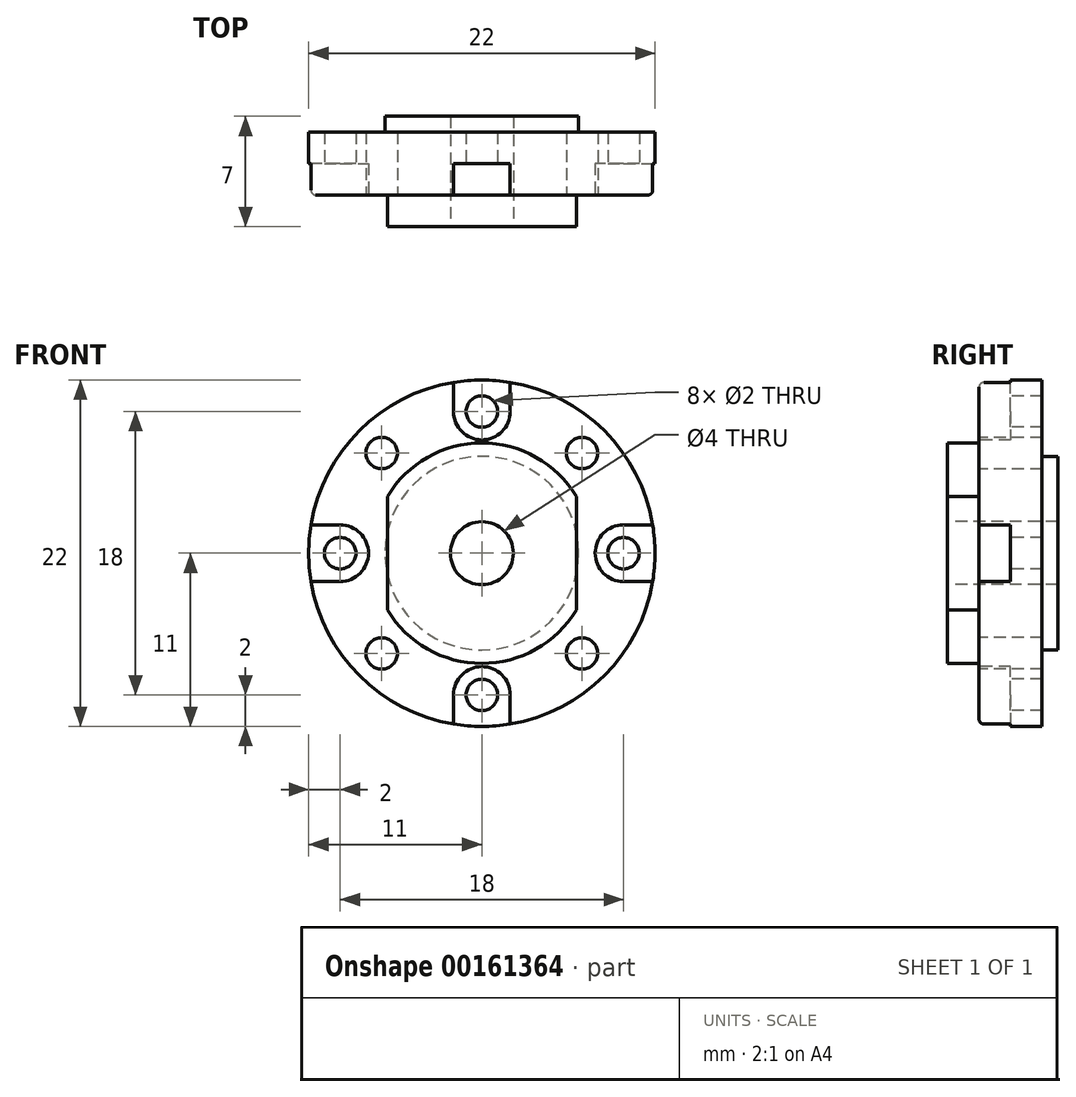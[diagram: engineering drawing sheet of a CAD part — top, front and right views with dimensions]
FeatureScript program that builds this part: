
annotation { "Feature Type Name" : "Feature", "Feature Type Description" : "" }
export const myFeature = defineFeature(function(context is Context, id is Id, definition is map)
    precondition{}
    {
        {
            var Q0;
            Q0=qCreatedBy(makeId("Front.planeOp"),FACE);
            var sketch = newSketch(context, id + "F0", { "sketchPlane" : qUnion([Q0])});
            skCircle(sketch, "E0", {"center": v(0, 0) * mm, "radius": 11 * mm});
            skSolve(sketch);
        }
        {
            var Q0;
            Q0=qSketchRegion(id+"F0",true);
            extrude(context, id + "F1", {"entities" : qUnion([Q0]), "depth" : 6 * mm});
        }
        {
            var Q0;
            Q0=makeQuery(id+"F1.opExtrude","CAP_FACE",FACE,{"disambiguationData":[OSD([sQuery(id+"F0.wireOp",EDGE,"E0")])],"isStart":false});
            var sketch = newSketch(context, id + "F2", { "sketchPlane" : qUnion([Q0])});
            skArc(sketch, "E1", {"start": v(-6, -3.6) * mm, "mid": v(0, -7) * mm, "end": v(6, -3.6) * mm});
            skCircle(sketch, "E2", {"center": v(0, 0) * mm, "radius": 16 * mm});
            skLineSegment(sketch, "E3", {"start": v(-6, 3.6) * mm, "end": v(-6, -3.6) * mm});
            skLineSegment(sketch, "E4", {"start": v(6, 3.6) * mm, "end": v(6, -3.6) * mm});
            skArc(sketch, "E5.trimOffspring", {"start": v(6, 3.6) * mm, "mid": v(0, 7) * mm, "end": v(-6, 3.6) * mm});
            skSolve(sketch);
        }
        {
            var Q0;
            Q0=qSketchRegion(id+"F2",true);
            extrude(context, id + "F3", {"entities" : qUnion([Q0]), "operationType" : NewBodyOperationType.REMOVE, "oppositeDirection" : true, "depth" : 2 * mm});
        }
        {
            var Q0;
            Q0=makeQuery(id+"F1.opExtrude","CAP_FACE",FACE,{"disambiguationData":[OSD([sQuery(id+"F0.wireOp",EDGE,"E0")])],"isStart":false});
            var sketch = newSketch(context, id + "F4", { "sketchPlane" : qUnion([Q0])});
            skCircle(sketch, "E6", {"center": v(0, 0) * mm, "radius": 2 * mm});
            skSolve(sketch);
        }
        {
            var Q0;
            Q0=makeQuery(id+"F3.boolean.opBoolean","COPY",FACE,{"derivedFrom":makeQuery(id+"F3.opExtrude","CAP_FACE",FACE,{"disambiguationData":[OSD([sQuery(id+"F2.wireOp",EDGE,"E1"),sQuery(id+"F2.wireOp",EDGE,"E2"),sQuery(id+"F2.wireOp",EDGE,"E3"),sQuery(id+"F2.wireOp",EDGE,"E4"),sQuery(id+"F2.wireOp",EDGE,"E5.trimOffspring")])],"isStart":false})});
            var sketch = newSketch(context, id + "F5", { "sketchPlane" : qUnion([Q0])});
            skLineSegment(sketch, "E7", {"start": v(0, 30.1) * mm, "end": v(0, -27.4) * mm, "construction": true});
            skLineSegment(sketch, "E8", {"start": v(-35.3, 0) * mm, "end": v(39.71, 0) * mm, "construction": true});
            skCircle(sketch, "E9", {"center": v(0, 9) * mm, "radius": 1 * mm});
            skLineSegment(sketch, "E10", {"start": v(-12.73, 12.73) * mm, "end": v(0, 0) * mm, "construction": true});
            skCircle(sketch, "E11", {"center": v(-6.36, 6.36) * mm, "radius": 1 * mm});
            skCircle(sketch, "E12.1.0", {"center": v(-9, 0) * mm, "radius": 1 * mm});
            skCircle(sketch, "E12.1.1", {"center": v(-6.36, -6.36) * mm, "radius": 1 * mm});
            skCircle(sketch, "E12.2.0", {"center": v(0, -9) * mm, "radius": 1 * mm});
            skCircle(sketch, "E12.2.1", {"center": v(6.36, -6.36) * mm, "radius": 1 * mm});
            skCircle(sketch, "E12.3.0", {"center": v(9, 0) * mm, "radius": 1 * mm});
            skCircle(sketch, "E12.3.1", {"center": v(6.36, 6.36) * mm, "radius": 1 * mm});
            skPoint(sketch, "E12.center", {"position": v(0, 0) * mm});
            skSolve(sketch);
        }
        {
            var Q0;
            Q0=qSketchRegion(id+"F5",true);
            extrude(context, id + "F6", {"entities" : qUnion([Q0]), "operationType" : NewBodyOperationType.REMOVE, "endBound" : BoundingType.THROUGH_ALL, "oppositeDirection" : true, "depth" : 25 * mm});
        }
        {
            var Q0;
            Q0=qCreatedBy(makeId("Front.planeOp"),FACE);
            var sketch = newSketch(context, id + "F7", { "sketchPlane" : qUnion([Q0])});
            skArc(sketch, "E13", {"start": v(-1.8, 9) * mm, "mid": v(0, 7.2) * mm, "end": v(1.8, 9) * mm});
            skLineSegment(sketch, "E14.top", {"start": v(-1.8, 11.65) * mm, "end": v(1.8, 11.65) * mm});
            skLineSegment(sketch, "E14.left", {"start": v(-1.8, 9) * mm, "end": v(-1.8, 11.65) * mm});
            skLineSegment(sketch, "E14.right", {"start": v(1.8, 9) * mm, "end": v(1.8, 11.65) * mm});
            skLineSegment(sketch, "E15.1.0", {"start": v(-9, -1.8) * mm, "end": v(-11.65, -1.8) * mm});
            skLineSegment(sketch, "E15.1.1", {"start": v(-11.65, -1.8) * mm, "end": v(-11.65, 1.8) * mm});
            skLineSegment(sketch, "E15.1.2", {"start": v(-9, 1.8) * mm, "end": v(-11.65, 1.8) * mm});
            skArc(sketch, "E15.1.3", {"start": v(-9, -1.8) * mm, "mid": v(-7.2, 0) * mm, "end": v(-9, 1.8) * mm});
            skLineSegment(sketch, "E15.2.0", {"start": v(1.8, -9) * mm, "end": v(1.8, -11.65) * mm});
            skLineSegment(sketch, "E15.2.1", {"start": v(1.8, -11.65) * mm, "end": v(-1.8, -11.65) * mm});
            skLineSegment(sketch, "E15.2.2", {"start": v(-1.8, -9) * mm, "end": v(-1.8, -11.65) * mm});
            skArc(sketch, "E15.2.3", {"start": v(1.8, -9) * mm, "mid": v(0, -7.2) * mm, "end": v(-1.8, -9) * mm});
            skLineSegment(sketch, "E15.3.0", {"start": v(9, 1.8) * mm, "end": v(11.65, 1.8) * mm});
            skLineSegment(sketch, "E15.3.1", {"start": v(11.65, 1.8) * mm, "end": v(11.65, -1.8) * mm});
            skLineSegment(sketch, "E15.3.2", {"start": v(9, -1.8) * mm, "end": v(11.65, -1.8) * mm});
            skArc(sketch, "E15.3.3", {"start": v(9, 1.8) * mm, "mid": v(7.2, 0) * mm, "end": v(9, -1.8) * mm});
            skPoint(sketch, "E15.center", {"position": v(0, 0) * mm});
            skSolve(sketch);
        }
        {
            var Q0;
            Q0=makeQuery(id+"F3.boolean.opBoolean","COPY",FACE,{"derivedFrom":makeQuery(id+"F3.opExtrude","CAP_FACE",FACE,{"disambiguationData":[OSD([sQuery(id+"F2.wireOp",EDGE,"E1"),sQuery(id+"F2.wireOp",EDGE,"E2"),sQuery(id+"F2.wireOp",EDGE,"E3"),sQuery(id+"F2.wireOp",EDGE,"E4"),sQuery(id+"F2.wireOp",EDGE,"E5.trimOffspring")])],"isStart":false})});
            var sketch = newSketch(context, id + "F8", { "sketchPlane" : qUnion([Q0])});
            skArc(sketch, "E16.0", {"start": v(-1.8, 9) * mm, "mid": v(0, 7.2) * mm, "end": v(1.8, 9) * mm});
            skLineSegment(sketch, "E16.1", {"start": v(-1.8, 11.65) * mm, "end": v(1.8, 11.65) * mm});
            skLineSegment(sketch, "E16.2", {"start": v(-1.8, 9) * mm, "end": v(-1.8, 11.65) * mm});
            skLineSegment(sketch, "E16.3", {"start": v(1.8, 9) * mm, "end": v(1.8, 11.65) * mm});
            skLineSegment(sketch, "E16.4", {"start": v(-9, -1.8) * mm, "end": v(-11.65, -1.8) * mm});
            skLineSegment(sketch, "E16.5", {"start": v(-11.65, -1.8) * mm, "end": v(-11.65, 1.8) * mm});
            skLineSegment(sketch, "E16.6", {"start": v(-9, 1.8) * mm, "end": v(-11.65, 1.8) * mm});
            skArc(sketch, "E16.7", {"start": v(-9, -1.8) * mm, "mid": v(-7.2, 0) * mm, "end": v(-9, 1.8) * mm});
            skLineSegment(sketch, "E16.8", {"start": v(1.8, -9) * mm, "end": v(1.8, -11.65) * mm});
            skLineSegment(sketch, "E16.9", {"start": v(1.8, -11.65) * mm, "end": v(-1.8, -11.65) * mm});
            skLineSegment(sketch, "E16.10", {"start": v(-1.8, -9) * mm, "end": v(-1.8, -11.65) * mm});
            skArc(sketch, "E16.11", {"start": v(1.8, -9) * mm, "mid": v(0, -7.2) * mm, "end": v(-1.8, -9) * mm});
            skLineSegment(sketch, "E16.12", {"start": v(9, 1.8) * mm, "end": v(11.65, 1.8) * mm});
            skLineSegment(sketch, "E16.13", {"start": v(11.65, 1.8) * mm, "end": v(11.65, -1.8) * mm});
            skLineSegment(sketch, "E16.14", {"start": v(9, -1.8) * mm, "end": v(11.65, -1.8) * mm});
            skArc(sketch, "E16.15", {"start": v(9, 1.8) * mm, "mid": v(7.2, 0) * mm, "end": v(9, -1.8) * mm});
            skPoint(sketch, "E16.16", {"position": v(0, 0) * mm});
            skSolve(sketch);
        }
        {
            var Q0;
            Q0=qSketchRegion(id+"F8",true);
            extrude(context, id + "F9", {"entities" : qUnion([Q0]), "operationType" : NewBodyOperationType.REMOVE, "oppositeDirection" : true, "depth" : 2 * mm});
        }
        {
            var Q0;
            {var subQ0=sQuery(id+"F2.wireOp",EDGE,"E2");Q0=makeQuery(id+"F9.boolean.opBoolean","SPLIT",EDGE,{"disambiguationData":[TD([makeQuery(id+"F9.opExtrude","SWEPT_FACE",FACE,{"disambiguationData":[OSD([sQuery(id+"F8.wireOp",EDGE,"E16.2")])]})])],"derivedFrom":makeQuery(id+"F3.boolean.opBoolean","COPY",EDGE,{"derivedFrom":makeQuery(id+"F3.opExtrude","CAP_EDGE",EDGE,{"disambiguationData":[OSD([subQ0])],"isStart":false})})});}
            var Q1;
            {var subQ0=sQuery(id+"F2.wireOp",EDGE,"E2");Q1=makeQuery(id+"F9.boolean.opBoolean","SPLIT",EDGE,{"disambiguationData":[TD([makeQuery(id+"F9.opExtrude","SWEPT_FACE",FACE,{"disambiguationData":[OSD([sQuery(id+"F8.wireOp",EDGE,"E16.3")])]})])],"derivedFrom":makeQuery(id+"F3.boolean.opBoolean","COPY",EDGE,{"derivedFrom":makeQuery(id+"F3.opExtrude","CAP_EDGE",EDGE,{"disambiguationData":[OSD([subQ0])],"isStart":false})})});}
            var Q2;
            {var subQ0=sQuery(id+"F2.wireOp",EDGE,"E2");Q2=makeQuery(id+"F9.boolean.opBoolean","SPLIT",EDGE,{"disambiguationData":[TD([makeQuery(id+"F9.opExtrude","SWEPT_FACE",FACE,{"disambiguationData":[OSD([sQuery(id+"F8.wireOp",EDGE,"E16.8")])]})])],"derivedFrom":makeQuery(id+"F3.boolean.opBoolean","COPY",EDGE,{"derivedFrom":makeQuery(id+"F3.opExtrude","CAP_EDGE",EDGE,{"disambiguationData":[OSD([subQ0])],"isStart":false})})});}
            var Q3;
            {var subQ0=sQuery(id+"F2.wireOp",EDGE,"E2");Q3=makeQuery(id+"F9.boolean.opBoolean","SPLIT",EDGE,{"disambiguationData":[TD([makeQuery(id+"F9.opExtrude","SWEPT_FACE",FACE,{"disambiguationData":[OSD([sQuery(id+"F8.wireOp",EDGE,"E16.4")])]})])],"derivedFrom":makeQuery(id+"F3.boolean.opBoolean","COPY",EDGE,{"derivedFrom":makeQuery(id+"F3.opExtrude","CAP_EDGE",EDGE,{"disambiguationData":[OSD([subQ0])],"isStart":false})})});}
            var Q4;
            Q4=makeQuery(id+"F3.boolean.opBoolean","COPY",EDGE,{"derivedFrom":makeQuery(id+"F3.opExtrude","CAP_EDGE",EDGE,{"disambiguationData":[OSD([sQuery(id+"F2.wireOp",EDGE,"E1")])],"isStart":true})});
            var Q5;
            Q5=makeQuery(id+"F3.boolean.opBoolean","COPY",EDGE,{"derivedFrom":makeQuery(id+"F3.opExtrude","CAP_EDGE",EDGE,{"disambiguationData":[OSD([sQuery(id+"F2.wireOp",EDGE,"E3")])],"isStart":true})});
            var Q6;
            Q6=makeQuery(id+"F3.boolean.opBoolean","COPY",EDGE,{"derivedFrom":makeQuery(id+"F3.opExtrude","CAP_EDGE",EDGE,{"disambiguationData":[OSD([sQuery(id+"F2.wireOp",EDGE,"E4")])],"isStart":true})});
            var Q7;
            Q7=makeQuery(id+"F3.boolean.opBoolean","COPY",EDGE,{"derivedFrom":makeQuery(id+"F3.opExtrude","CAP_EDGE",EDGE,{"disambiguationData":[OSD([sQuery(id+"F2.wireOp",EDGE,"E5.trimOffspring")])],"isStart":true})});
            var Q8;
            {var subQ0=makeQuery(id+"F1.opExtrude","SWEPT_FACE",FACE,{"disambiguationData":[OSD([sQuery(id+"F0.wireOp",EDGE,"E0")])]});var subQ1=makeQuery(id+"F3.opExtrude","CAP_FACE",FACE,{"disambiguationData":[OSD([sQuery(id+"F2.wireOp",EDGE,"E1"),sQuery(id+"F2.wireOp",EDGE,"E2"),sQuery(id+"F2.wireOp",EDGE,"E3"),sQuery(id+"F2.wireOp",EDGE,"E4"),sQuery(id+"F2.wireOp",EDGE,"E5.trimOffspring")])],"isStart":false});Q8=makeQuery(id+"F9.boolean.opBoolean","SPLIT",EDGE,{"disambiguationData":[TD([makeQuery(id+"F9.opExtrude","SWEPT_FACE",FACE,{"disambiguationData":[OSD([sQuery(id+"F8.wireOp",EDGE,"E16.8")])]})])],"derivedFrom":makeQuery(id+"F3.boolean.opBoolean","INTERSECT",EDGE,{"derivedFrom":[subQ0,subQ1]})});}
            var Q9;
            {var subQ0=makeQuery(id+"F1.opExtrude","SWEPT_FACE",FACE,{"disambiguationData":[OSD([sQuery(id+"F0.wireOp",EDGE,"E0")])]});var subQ1=makeQuery(id+"F3.opExtrude","CAP_FACE",FACE,{"disambiguationData":[OSD([sQuery(id+"F2.wireOp",EDGE,"E1"),sQuery(id+"F2.wireOp",EDGE,"E2"),sQuery(id+"F2.wireOp",EDGE,"E3"),sQuery(id+"F2.wireOp",EDGE,"E4"),sQuery(id+"F2.wireOp",EDGE,"E5.trimOffspring")])],"isStart":false});Q9=makeQuery(id+"F9.boolean.opBoolean","SPLIT",EDGE,{"disambiguationData":[TD([makeQuery(id+"F9.opExtrude","SWEPT_FACE",FACE,{"disambiguationData":[OSD([sQuery(id+"F8.wireOp",EDGE,"E16.4")])]})])],"derivedFrom":makeQuery(id+"F3.boolean.opBoolean","INTERSECT",EDGE,{"derivedFrom":[subQ0,subQ1]})});}
            var Q10;
            {var subQ0=makeQuery(id+"F1.opExtrude","SWEPT_FACE",FACE,{"disambiguationData":[OSD([sQuery(id+"F0.wireOp",EDGE,"E0")])]});var subQ1=makeQuery(id+"F3.opExtrude","CAP_FACE",FACE,{"disambiguationData":[OSD([sQuery(id+"F2.wireOp",EDGE,"E1"),sQuery(id+"F2.wireOp",EDGE,"E2"),sQuery(id+"F2.wireOp",EDGE,"E3"),sQuery(id+"F2.wireOp",EDGE,"E4"),sQuery(id+"F2.wireOp",EDGE,"E5.trimOffspring")])],"isStart":false});Q10=makeQuery(id+"F9.boolean.opBoolean","SPLIT",EDGE,{"disambiguationData":[TD([makeQuery(id+"F9.opExtrude","SWEPT_FACE",FACE,{"disambiguationData":[OSD([sQuery(id+"F8.wireOp",EDGE,"E16.2")])]})])],"derivedFrom":makeQuery(id+"F3.boolean.opBoolean","INTERSECT",EDGE,{"derivedFrom":[subQ0,subQ1]})});}
            var Q11;
            {var subQ0=makeQuery(id+"F1.opExtrude","SWEPT_FACE",FACE,{"disambiguationData":[OSD([sQuery(id+"F0.wireOp",EDGE,"E0")])]});var subQ1=makeQuery(id+"F3.opExtrude","CAP_FACE",FACE,{"disambiguationData":[OSD([sQuery(id+"F2.wireOp",EDGE,"E1"),sQuery(id+"F2.wireOp",EDGE,"E2"),sQuery(id+"F2.wireOp",EDGE,"E3"),sQuery(id+"F2.wireOp",EDGE,"E4"),sQuery(id+"F2.wireOp",EDGE,"E5.trimOffspring")])],"isStart":false});Q11=makeQuery(id+"F9.boolean.opBoolean","SPLIT",EDGE,{"disambiguationData":[TD([makeQuery(id+"F9.opExtrude","SWEPT_FACE",FACE,{"disambiguationData":[OSD([sQuery(id+"F8.wireOp",EDGE,"E16.3")])]})])],"derivedFrom":makeQuery(id+"F3.boolean.opBoolean","INTERSECT",EDGE,{"derivedFrom":[subQ0,subQ1]})});}
            fillet(context, id + "F10", {"entities" : qUnion([Q0, Q1, Q2, Q3, Q4, Q5, Q6, Q7, Q8, Q9, Q10, Q11]), "radius" : 0.3 * mm, "tangentPropagation" : true, "allowEdgeOverflow" : false});
        }
        {
            var Q0;
            Q0=makeQuery(id+"F1.opExtrude","CAP_FACE",FACE,{"disambiguationData":[OSD([sQuery(id+"F0.wireOp",EDGE,"E0")])],"isStart":true});
            var sketch = newSketch(context, id + "F11", { "sketchPlane" : qUnion([Q0])});
            skCircle(sketch, "E17", {"center": v(0, 0) * mm, "radius": 6.15 * mm});
            skSolve(sketch);
        }
        {
            var Q0;
            Q0 = qSketchRegion(id + "F11", true);
            extrude(context, id + "F12", {"entities" : qUnion([Q0]), "operationType" : NewBodyOperationType.ADD, "depth" : 1 * mm});
        }
        {
            var Q0;
            Q0 = qSketchRegion(id + "F4", true);
            extrude(context, id + "F13", {"entities" : qUnion([Q0]), "operationType" : NewBodyOperationType.REMOVE, "endBound" : BoundingType.THROUGH_ALL, "oppositeDirection" : true, "depth" : 25 * mm});
        }
    });
